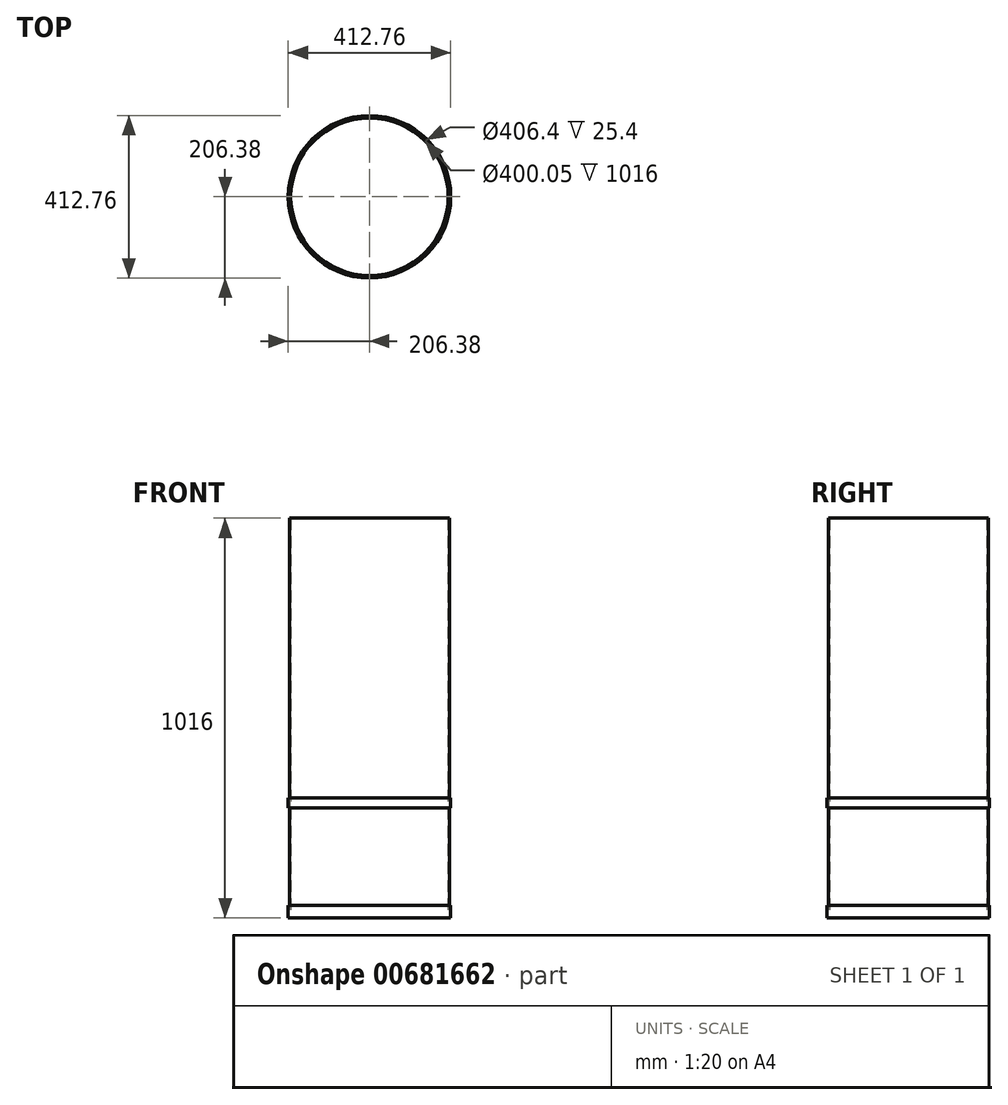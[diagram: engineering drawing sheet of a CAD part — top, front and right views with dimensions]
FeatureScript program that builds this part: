
annotation { "Feature Type Name" : "Feature", "Feature Type Description" : "" }
export const myFeature = defineFeature(function(context is Context, id is Id, definition is map)
    precondition{}
    {
        {
            var Q0;
            Q0=qCreatedBy(makeId("Top.planeOp"),FACE);
            var sketch = newSketch(context, id + "F0", { "sketchPlane" : qUnion([Q0])});
            skCircle(sketch, "E0", {"center": v(0, 0) * mm, "radius": 203.2 * mm});
            skCircle(sketch, "E1", {"center": v(0, 0) * mm, "radius": 200.03 * mm});
            skCircle(sketch, "E2", {"center": v(0, 0) * mm, "radius": 206.38 * mm});
            skSolve(sketch);
        }
        {
            var Q0;
            Q0=makeQuery(id+"F0.imprint","IMPRINT",FACE,{"disambiguationData":[TD([[makeQuery(id+"F0.imprint","IMPRINT",EDGE,{"derivedFrom":sQuery(id+"F0.wireOp",EDGE,"E0")}),1.0]])]});
            extrude(context, id + "F1", {"entities" : qUnion([Q0]), "depth" : 1016 * mm, "offsetDistance" : 25.4 * mm});
        }
        {
            var Q0;
            Q0=makeQuery(id+"F0.imprint","IMPRINT",FACE,{"disambiguationData":[TD([[makeQuery(id+"F0.imprint","IMPRINT",EDGE,{"derivedFrom":sQuery(id+"F0.wireOp",EDGE,"E0")}),-1.0]])]});
            extrude(context, id + "F2", {"entities" : qUnion([Q0]), "operationType" : NewBodyOperationType.ADD, "depth" : 31.75 * mm, "offsetDistance" : 25.4 * mm});
        }
        {
            var Q0;
            Q0=qCreatedBy(makeId("Front.planeOp"),FACE);
            var sketch = newSketch(context, id + "F3", { "sketchPlane" : qUnion([Q0])});
            skLineSegment(sketch, "E3", {"start": v(0, 0) * mm, "end": v(0, 279.4) * mm});
            skLineSegment(sketch, "E4", {"start": v(0, 279.4) * mm, "end": v(-203.2, 279.4) * mm});
            skSolve(sketch);
        }
        {
            var Q0;
            Q0=sQuery(id+"F3.wireOp",EDGE,"E4");
            cPlane(context, id + "F4", {"entities" : qUnion([Q0]), "cplaneType" : CPlaneType.LINE_ANGLE, "offset" : 25.4 * mm, "angle" : 90 * degree, "width" : 152.4 * mm, "height" : 152.4 * mm});
        }
        {
            var Q0;
            Q0=qCreatedBy(id+"F4.planeOp",FACE);
            var sketch = newSketch(context, id + "F5", { "sketchPlane" : qUnion([Q0])});
            skCircle(sketch, "E5", {"center": v(0, 0) * mm, "radius": 203.2 * mm});
            skCircle(sketch, "E6", {"center": v(0, 0) * mm, "radius": 206.38 * mm});
            skSolve(sketch);
        }
        {
            var Q0;
            Q0=makeQuery(id+"F5.imprint","IMPRINT",FACE,{"disambiguationData":[TD([[makeQuery(id+"F5.imprint","IMPRINT",EDGE,{"derivedFrom":sQuery(id+"F5.wireOp",EDGE,"E5")}),-1.0]])]});
            extrude(context, id + "F6", {"entities" : qUnion([Q0]), "depth" : 25.4 * mm, "offsetDistance" : 25.4 * mm});
        }
    });
